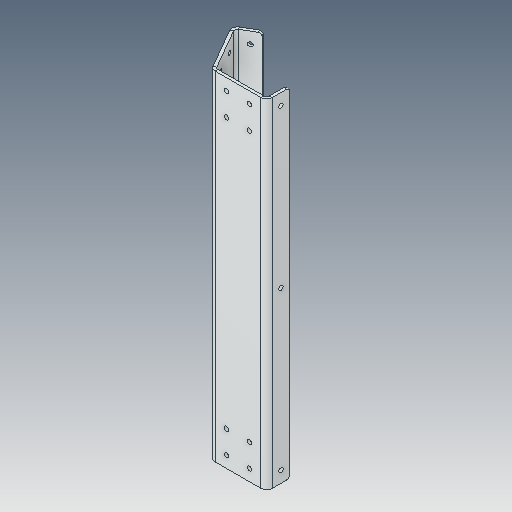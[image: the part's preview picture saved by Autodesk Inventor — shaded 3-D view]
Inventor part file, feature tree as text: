
AUTODESK INVENTOR PART (.ipt)
format: ipt  version: 2023.5 (Build 275446000, 446)  size: 126,976 bytes
history: native  units: in
note: dims shown in document units (in); Inventor stores cm internally (conversion verified against a paired STEP export)
features: fillet x1
ambient origin geometry x8: Origin, YZ Plane, XZ Plane, XY Plane, X Axis, Y Axis, Z Axis, Center Point
bodies: Solid1 (feature_tree)
feature tree (1):
  fillet  "Fillet1"  [1 undecoded]
note: 1 required parameter value undecoded (feature->parameter linkage not recoverable at this tier; creation-order binding heuristic only, values carry confidence <= 0.55)
